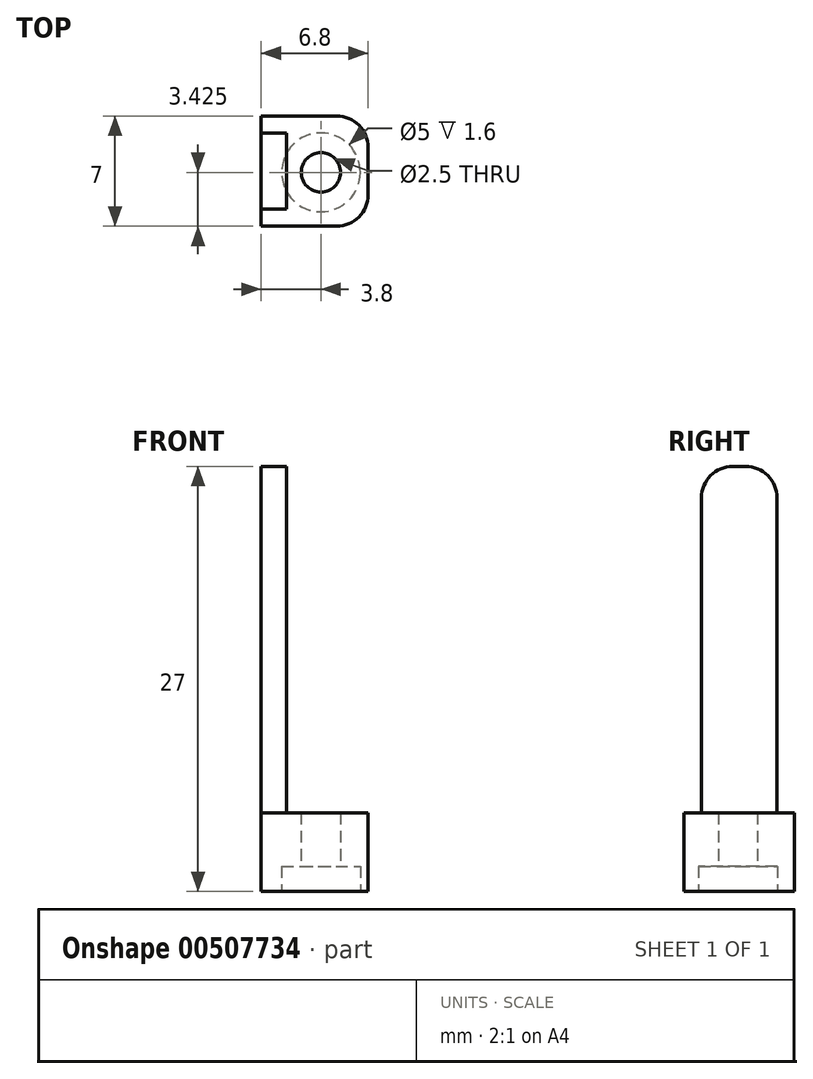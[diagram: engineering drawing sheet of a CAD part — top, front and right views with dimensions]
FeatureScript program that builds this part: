
annotation { "Feature Type Name" : "Feature", "Feature Type Description" : "" }
export const myFeature = defineFeature(function(context is Context, id is Id, definition is map)
    precondition{}
    {
        {
            var Q0;
            Q0=qCreatedBy(makeId("Top.planeOp"),FACE);
            var sketch = newSketch(context, id + "F0", { "sketchPlane" : qUnion([Q0])});
            skLineSegment(sketch, "E0.bottom", {"start": v(-4, 21.81) * mm, "end": v(1, 21.81) * mm});
            skLineSegment(sketch, "E0.top", {"start": v(-4, 14.81) * mm, "end": v(1, 14.81) * mm});
            skLineSegment(sketch, "E0.left", {"start": v(3, 16.81) * mm, "end": v(3, 19.81) * mm});
            skLineSegment(sketch, "E0.right", {"start": v(-4, 14.81) * mm, "end": v(-4, 21.81) * mm});
            skPoint(sketch, "E1.visualSharp", {"position": v(3, 21.81) * mm});
            skArc(sketch, "E1.filletArc", {"start": v(3, 19.81) * mm, "mid": v(2.41, 21.23) * mm, "end": v(1, 21.81) * mm});
            skPoint(sketch, "E2.visualSharp", {"position": v(3, 14.81) * mm});
            skArc(sketch, "E2.filletArc", {"start": v(1, 14.81) * mm, "mid": v(2.41, 15.4) * mm, "end": v(3, 16.81) * mm});
            skSolve(sketch);
        }
        {
            var Q0;
            Q0=makeQuery(id+"F0.imprint","IMPRINT",FACE,{"disambiguationData":[TD([[makeQuery(id+"F0.imprint","IMPRINT",EDGE,{"derivedFrom":sQuery(id+"F0.wireOp",EDGE,"E0.bottom")}),-1.0]])]});
            var Q1;
            Q1=makeQuery(id+"F0.imprint","IMPRINT",FACE,{"disambiguationData":[TD([[makeQuery(id+"F0.imprint","IMPRINT",EDGE,{"derivedFrom":sQuery(id+"F0.wireOp",EDGE,"OGHk75Aa-BJnh-hkSo-yNRI-ETdDBhqNUhSb")}),1.0]])]});
            var Q2;
            Q2=makeQuery(id+"F0.imprint","IMPRINT",FACE,{"disambiguationData":[TD([[makeQuery(id+"F0.imprint","IMPRINT",EDGE,{"derivedFrom":sQuery(id+"F0.wireOp",EDGE,"Jd6CkG7M-QaOW-uCvP-q8XN-jmcHcbD0AcgO")}),1.0]])]});
            extrude(context, id + "F1", {"entities" : qUnion([Q0, Q1, Q2]), "depth" : 5 * mm, "offsetDistance" : 25 * mm});
        }
        {
            var Q0;
            Q0=makeQuery(id+"F1.opExtrude","CAP_FACE",FACE,{"disambiguationData":[OSD([sQuery(id+"F0.wireOp",EDGE,"E0.bottom"),sQuery(id+"F0.wireOp",EDGE,"E0.top"),sQuery(id+"F0.wireOp",EDGE,"E0.left"),sQuery(id+"F0.wireOp",EDGE,"E0.right"),sQuery(id+"F0.wireOp",EDGE,"E1.filletArc"),sQuery(id+"F0.wireOp",EDGE,"E2.filletArc")])],"isStart":true});
            var sketch = newSketch(context, id + "F2", { "sketchPlane" : qUnion([Q0])});
            skCircle(sketch, "E3", {"center": v(0, -18.23) * mm, "radius": 2.5 * mm});
            skSolve(sketch);
        }
        {
            var Q0;
            Q0 = qSketchRegion(id + "F2", true);
            extrude(context, id + "F3", {"entities" : qUnion([Q0]), "operationType" : NewBodyOperationType.REMOVE, "oppositeDirection" : true, "depth" : 1.6 * mm, "offsetDistance" : 25 * mm});
        }
        {
            var Q0;
            Q0=makeQuery(id+"F3.boolean.opBoolean","COPY",FACE,{"derivedFrom":makeQuery(id+"F3.opExtrude","CAP_FACE",FACE,{"disambiguationData":[OSD([sQuery(id+"F2.wireOp",EDGE,"E3")])],"isStart":false})});
            var sketch = newSketch(context, id + "F4", { "sketchPlane" : qUnion([Q0])});
            skCircle(sketch, "E4", {"center": v(0, -18.23) * mm, "radius": 1.25 * mm});
            skSolve(sketch);
        }
        {
            var Q0;
            Q0 = qSketchRegion(id + "F4", true);
            extrude(context, id + "F5", {"entities" : qUnion([Q0]), "operationType" : NewBodyOperationType.REMOVE, "oppositeDirection" : true, "depth" : 3.4 * mm, "offsetDistance" : 25 * mm});
        }
        {
            var Q0;
            Q0=makeQuery(id+"F1.opExtrude","CAP_FACE",FACE,{"disambiguationData":[OSD([sQuery(id+"F0.wireOp",EDGE,"E0.bottom"),sQuery(id+"F0.wireOp",EDGE,"E0.top"),sQuery(id+"F0.wireOp",EDGE,"E0.left"),sQuery(id+"F0.wireOp",EDGE,"E0.right"),sQuery(id+"F0.wireOp",EDGE,"E1.filletArc"),sQuery(id+"F0.wireOp",EDGE,"E2.filletArc")])],"isStart":false});
            var sketch = newSketch(context, id + "F6", { "sketchPlane" : qUnion([Q0])});
            skLineSegment(sketch, "E5.bottom", {"start": v(-4, 20.71) * mm, "end": v(-2, 20.71) * mm});
            skLineSegment(sketch, "E5.top", {"start": v(-4, 15.91) * mm, "end": v(-2, 15.91) * mm});
            skLineSegment(sketch, "E5.left", {"start": v(-4, 20.71) * mm, "end": v(-4, 15.91) * mm});
            skLineSegment(sketch, "E5.right", {"start": v(-2, 20.71) * mm, "end": v(-2, 15.91) * mm});
            skSolve(sketch);
        }
        {
            var Q0;
            Q0 = qSketchRegion(id + "F6", true);
            extrude(context, id + "F7", {"entities" : qUnion([Q0]), "operationType" : NewBodyOperationType.ADD, "depth" : 22 * mm, "offsetDistance" : 25 * mm});
        }
        {
            var Q0;
            Q0=makeQuery(id+"F7.opExtrude","CAP_EDGE",EDGE,{"disambiguationData":[OSD([sQuery(id+"F6.wireOp",EDGE,"E5.bottom")])],"isStart":false});
            var Q1;
            Q1=makeQuery(id+"F7.opExtrude","CAP_EDGE",EDGE,{"disambiguationData":[OSD([sQuery(id+"F6.wireOp",EDGE,"E5.top")])],"isStart":false});
            fillet(context, id + "F8", {"entities" : qUnion([Q0, Q1]), "radius" : 2 * mm, "tangentPropagation" : true, "allowEdgeOverflow" : false});
        }
        {
            var Q0;
            Q0=makeQuery(id+"F7.opExtrude","SWEPT_FACE",FACE,{"disambiguationData":[OSD([sQuery(id+"F6.wireOp",EDGE,"E5.right")])]});
            extrude(context, id + "F9", {"entities" : qUnion([Q0]), "operationType" : NewBodyOperationType.REMOVE, "oppositeDirection" : true, "depth" : 0.2 * mm, "offsetDistance" : 25 * mm});
        }
        {
            var Q0;
            Q0=makeQuery(id+"F7.boolean.opBoolean","MERGE",FACE,{"derivedFrom":[makeQuery(id+"F1.opExtrude","SWEPT_FACE",FACE,{"disambiguationData":[OSD([sQuery(id+"F0.wireOp",EDGE,"E0.right")])]}),makeQuery(id+"F7.opExtrude","SWEPT_FACE",FACE,{"disambiguationData":[OSD([sQuery(id+"F6.wireOp",EDGE,"E5.left")])]})]});
            extrude(context, id + "F10", {"entities" : qUnion([Q0]), "operationType" : NewBodyOperationType.REMOVE, "oppositeDirection" : true, "depth" : 0.2 * mm, "offsetDistance" : 25 * mm});
        }
    });
